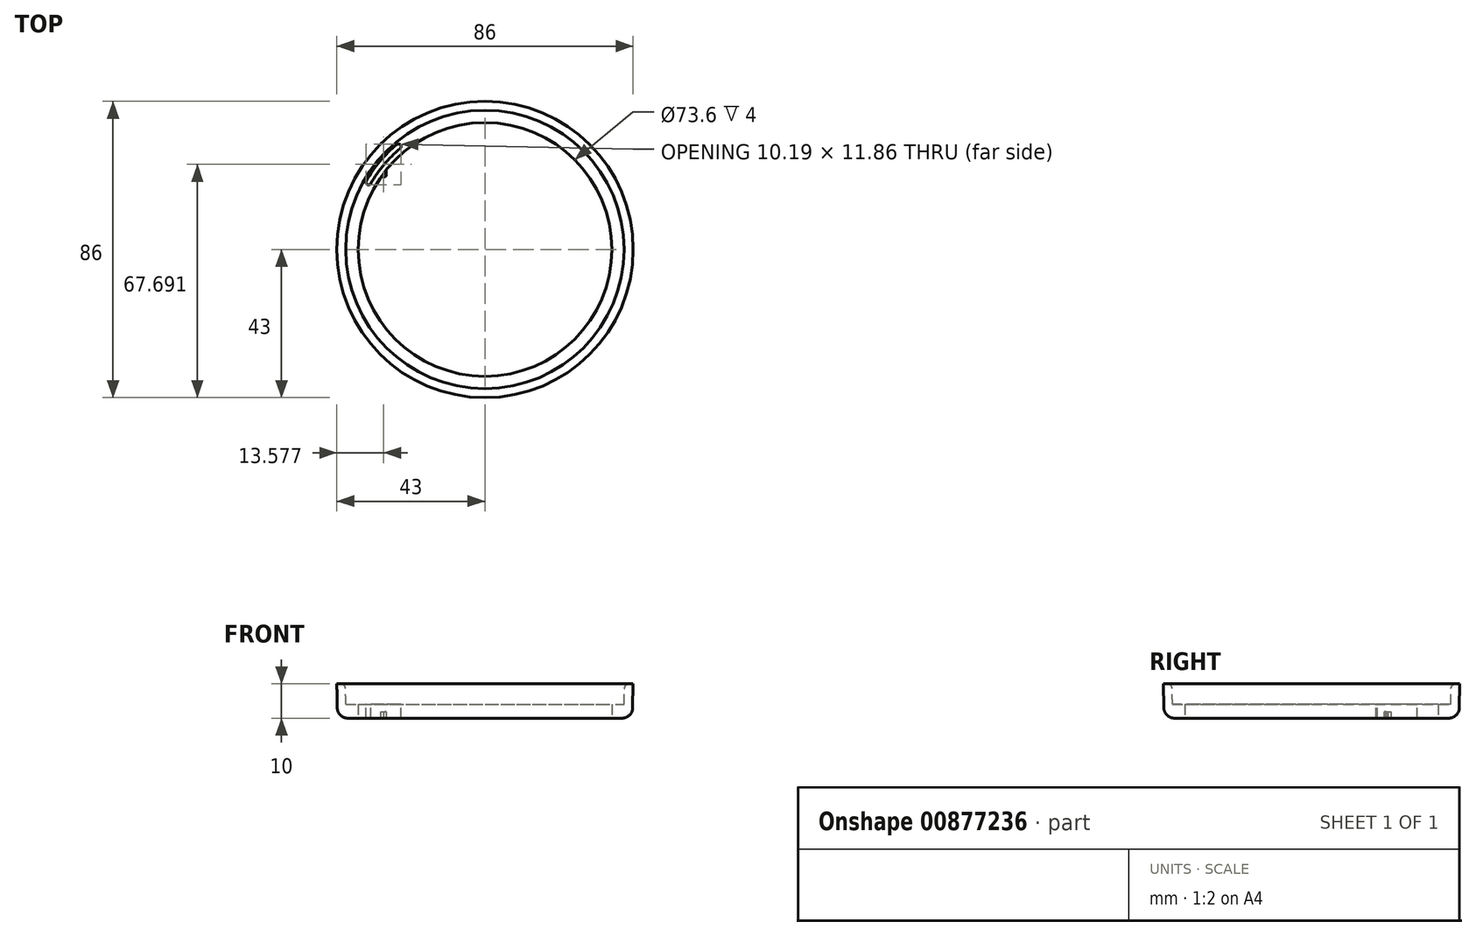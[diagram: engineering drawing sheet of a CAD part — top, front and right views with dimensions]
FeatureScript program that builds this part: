
annotation { "Feature Type Name" : "Feature", "Feature Type Description" : "" }
export const myFeature = defineFeature(function(context is Context, id is Id, definition is map)
    precondition{}
    {
        {
            var Q0;
            Q0=qCreatedBy(makeId("Front.planeOp"),FACE);
            var sketch = newSketch(context, id + "F0", { "sketchPlane" : qUnion([Q0])});
            skLineSegment(sketch, "E0", {"start": v(-42.86, 2.94) * mm, "end": v(-43, 10) * mm});
            skLineSegment(sketch, "E1", {"start": v(-43, 10) * mm, "end": v(-41.97, 10) * mm});
            skLineSegment(sketch, "E2", {"start": v(-40.47, 8.53) * mm, "end": v(-40.38, 4) * mm});
            skLineSegment(sketch, "E3", {"start": v(-40.38, 4) * mm, "end": v(-36.8, 4) * mm});
            skLineSegment(sketch, "E4", {"start": v(-36.8, 4) * mm, "end": v(-36.8, 0) * mm});
            skLineSegment(sketch, "E5", {"start": v(-36.8, 0) * mm, "end": v(-39.86, 0) * mm});
            skLineSegment(sketch, "E6", {"start": v(0, 0) * mm, "end": v(0, 62.72) * mm, "construction": true});
            skPoint(sketch, "E7.visualSharp", {"position": v(-42.8, 0) * mm});
            skArc(sketch, "E7.filletArc", {"start": v(-42.86, 2.94) * mm, "mid": v(-41.96, 0.86) * mm, "end": v(-39.86, 0) * mm});
            skPoint(sketch, "E8.visualSharp", {"position": v(-40.5, 10) * mm});
            skArc(sketch, "E8.filletArc", {"start": v(-40.47, 8.53) * mm, "mid": v(-40.92, 9.57) * mm, "end": v(-41.97, 10) * mm});
            skSolve(sketch);
        }
        {
            var Q0;
            Q0=qSketchRegion(id+"F0",true);
            var Q1;
            Q1=sQuery(id+"F0.wireOp",EDGE,"E6");
            revolve(context, id + "F1", {"entities" : qUnion([Q0]), "axis" : qUnion([Q1]), "revolveType" : RevolveType.FULL});
        }
        {
            var Q0;
            Q0=makeQuery(id+"F1.opRevolve","SWEPT_FACE",FACE,{"disambiguationData":[OSD([sQuery(id+"F0.wireOp",EDGE,"E3")])]});
            var sketch = newSketch(context, id + "F2", { "sketchPlane" : qUnion([Q0])});
            skLineSegment(sketch, "E9", {"start": v(-18.25, 30.04) * mm, "end": v(-19.1, 31.45) * mm});
            skLineSegment(sketch, "E10", {"start": v(0, 0) * mm, "end": v(-18.25, 30.04) * mm, "construction": true});
            skArc(sketch, "E11", {"start": v(-18.25, 30.04) * mm, "mid": v(-0.51, -35.15) * mm, "end": v(19.12, 29.5) * mm, "construction": true});
            skArc(sketch, "E12", {"start": v(19.1, 31.45) * mm, "mid": v(-19.56, -31.17) * mm, "end": v(20.02, 30.88) * mm});
            skArc(sketch, "E13", {"start": v(20.02, 30.88) * mm, "mid": v(0.54, 36.8) * mm, "end": v(-19.1, 31.45) * mm});
            skLineSegment(sketch, "E14", {"start": v(0, 0) * mm, "end": v(0, 32.81) * mm, "construction": true});
            skArc(sketch, "E15.0", {"start": v(-3.13, 35.16) * mm, "mid": v(-8.6, 34.24) * mm, "end": v(-13.87, 32.46) * mm});
            skLineSegment(sketch, "E16", {"start": v(-13.87, 32.46) * mm, "end": v(-13.83, 32.37) * mm});
            skLineSegment(sketch, "E17", {"start": v(-13.83, 32.37) * mm, "end": v(0, 0) * mm, "construction": true});
            skArc(sketch, "E18.trimOffspring", {"start": v(-13.83, 32.37) * mm, "mid": v(-16.08, 31.29) * mm, "end": v(-18.25, 30.04) * mm});
            skLineSegment(sketch, "E19", {"start": v(0, 32.81) * mm, "end": v(0, 36.8) * mm, "construction": true});
            skArc(sketch, "E20", {"start": v(0, 36.8) * mm, "mid": v(-1.76, 36.37) * mm, "end": v(-3.13, 35.16) * mm});
            skPoint(sketch, "E21", {"position": v(-3.12, 35.16) * mm});
            skLineSegment(sketch, "E22.MirrorCS", {"start": v(18.25, 30.04) * mm, "end": v(19.1, 31.45) * mm});
            skArc(sketch, "E23.MirrorCS", {"start": v(-20.02, 30.88) * mm, "mid": v(-0.54, 36.8) * mm, "end": v(19.1, 31.45) * mm});
            skArc(sketch, "E24.MirrorCS", {"start": v(3.13, 35.16) * mm, "mid": v(8.6, 34.24) * mm, "end": v(13.87, 32.46) * mm});
            skArc(sketch, "E25.MirrorCS", {"start": v(13.83, 32.37) * mm, "mid": v(16.08, 31.29) * mm, "end": v(18.25, 30.04) * mm});
            skLineSegment(sketch, "E26.MirrorCS", {"start": v(13.87, 32.46) * mm, "end": v(13.83, 32.37) * mm});
            skArc(sketch, "E27.MirrorCS", {"start": v(0, 36.8) * mm, "mid": v(1.76, 36.37) * mm, "end": v(3.13, 35.16) * mm});
            skLineSegment(sketch, "E28", {"start": v(-20.16, 30.78) * mm, "end": v(-20.03, 29.99) * mm});
            skLineSegment(sketch, "E29", {"start": v(-20.51, 29.4) * mm, "end": v(-22.2, 29.34) * mm});
            skArc(sketch, "E30.0", {"start": v(19.1, 31.45) * mm, "mid": v(0, 36.8) * mm, "end": v(-19.1, 31.45) * mm});
            skArc(sketch, "E31.trimOffspring", {"start": v(-20.16, 30.78) * mm, "mid": v(-21.2, 30.08) * mm, "end": v(-22.2, 29.34) * mm});
            skPoint(sketch, "E32.visualSharp", {"position": v(-19.94, 29.43) * mm});
            skArc(sketch, "E32.filletArc", {"start": v(-20.51, 29.4) * mm, "mid": v(-20.14, 29.59) * mm, "end": v(-20.03, 29.99) * mm});
            skSolve(sketch);
        }
        {
            var Q0;
            Q0=makeQuery(id+"F1.opRevolve","SWEPT_FACE",FACE,{"disambiguationData":[OSD([sQuery(id+"F0.wireOp",EDGE,"E5")])]});
            var sketch = newSketch(context, id + "F3", { "sketchPlane" : qUnion([Q0])});
            skLineSegment(sketch, "E33", {"start": v(0, 0) * mm, "end": v(-36.8, 0) * mm, "construction": true});
            skArc(sketch, "E34.0", {"start": v(-35.3, 0) * mm, "mid": v(-35.25, -1.8) * mm, "end": v(-35.12, -3.6) * mm, "construction": true});
            skLineSegment(sketch, "E35", {"start": v(0, 0) * mm, "end": v(-29.59, 19.25) * mm, "construction": true});
            skLineSegment(sketch, "E36", {"start": v(-29.59, 19.25) * mm, "end": v(-30.85, 20.07) * mm});
            skCircle(sketch, "E37.0", {"center": v(0, 0) * mm, "radius": 36.8 * mm});
            skArc(sketch, "E38.0", {"start": v(-30.84, 17.68) * mm, "mid": v(-33.92, 10.65) * mm, "end": v(-35.41, 3.12) * mm});
            skLineSegment(sketch, "E39", {"start": v(-30.63, 17.54) * mm, "end": v(-30.84, 17.68) * mm});
            skArc(sketch, "E40", {"start": v(-35.41, 3.12) * mm, "mid": v(-36.44, 1.7) * mm, "end": v(-36.8, 0) * mm});
            skArc(sketch, "E41.trimOffspring", {"start": v(-35.41, -3.13) * mm, "mid": v(34.5, -8.6) * mm, "end": v(-29.8, 19.39) * mm, "construction": true});
            skLineSegment(sketch, "E42", {"start": v(-29.59, 19.25) * mm, "end": v(-29.59, 19.25) * mm});
            skArc(sketch, "E43", {"start": v(-29.59, 19.25) * mm, "mid": v(-30.12, 18.4) * mm, "end": v(-30.63, 17.54) * mm});
            skArc(sketch, "E44.MirrorCS", {"start": v(-35.3, 0) * mm, "mid": v(33.84, 10.04) * mm, "end": v(-29.59, -19.25) * mm, "construction": true});
            skArc(sketch, "E45.MirrorCS", {"start": v(-30.84, -17.68) * mm, "mid": v(-33.92, -10.65) * mm, "end": v(-35.41, -3.13) * mm});
            skLineSegment(sketch, "E46.MirrorCS", {"start": v(-29.59, -19.25) * mm, "end": v(-30.85, -20.07) * mm});
            skArc(sketch, "E47.MirrorCS", {"start": v(-29.59, -19.25) * mm, "mid": v(-30.12, -18.4) * mm, "end": v(-30.63, -17.54) * mm});
            skLineSegment(sketch, "E48.MirrorCS", {"start": v(-30.63, -17.54) * mm, "end": v(-30.84, -17.68) * mm});
            skArc(sketch, "E49.MirrorCS", {"start": v(-35.41, -3.12) * mm, "mid": v(-36.44, -1.7) * mm, "end": v(-36.8, 0) * mm});
            skArc(sketch, "E50.trimOffspring", {"start": v(-30.63, -17.54) * mm, "mid": v(35.29, -1) * mm, "end": v(-29.59, 19.25) * mm, "construction": true});
            skLineSegment(sketch, "E51", {"start": v(-30.15, -21.1) * mm, "end": v(-29.12, -21.1) * mm});
            skLineSegment(sketch, "E52", {"start": v(-28.62, -21.61) * mm, "end": v(-28.64, -23.1) * mm});
            skPoint(sketch, "E53.visualSharp", {"position": v(-28.6, -21.1) * mm});
            skArc(sketch, "E53.filletArc", {"start": v(-28.62, -21.61) * mm, "mid": v(-28.76, -21.25) * mm, "end": v(-29.12, -21.1) * mm});
            skArc(sketch, "E54", {"start": v(-30.85, 20.07) * mm, "mid": v(36.75, 1.87) * mm, "end": v(-28.64, -23.1) * mm, "construction": true});
            skArc(sketch, "E55", {"start": v(-30.85, -20.07) * mm, "mid": v(-36.8, 0) * mm, "end": v(-30.85, 20.07) * mm});
            skArc(sketch, "E56", {"start": v(-30.15, -21.1) * mm, "mid": v(-30.5, -20.59) * mm, "end": v(-30.85, -20.07) * mm, "construction": true});
            skArc(sketch, "E57", {"start": v(-28.64, -23.1) * mm, "mid": v(-29.41, -22.12) * mm, "end": v(-30.15, -21.1) * mm});
            skSolve(sketch);
        }
        {
            var Q0;
            {var subQ1=sQuery(id+"F3.wireOp",EDGE,"E36");Q0=makeQuery(id+"F3.imprint","IMPRINT",FACE,{"disambiguationData":[TD([[makeQuery(id+"F3.imprint","IMPRINT",EDGE,{"derivedFrom":subQ1}),1.0]])]});}
            var Q1;
            Q1=makeQuery(id+"F3.imprint","IMPRINT",FACE,{"disambiguationData":[TD([[makeQuery(id+"F3.imprint","IMPRINT",EDGE,{"derivedFrom":sQuery(id+"F3.wireOp",EDGE,"E45.MirrorCS")}),1.0]])]});
            var Q2;
            {var subQ0=sQuery(id+"F3.wireOp",EDGE,"E51");Q2=makeQuery(id+"F3.imprint","IMPRINT",FACE,{"disambiguationData":[TD([[makeQuery(id+"F3.imprint","IMPRINT",EDGE,{"derivedFrom":subQ0}),-1.0]])]});}
            extrude(context, id + "F4", {"entities" : qUnion([Q0, Q1, Q2]), "operationType" : NewBodyOperationType.ADD, "oppositeDirection" : true, "offsetDistance" : 25 * mm, "depth" : 1.8 * mm});
        }
        {
            var Q0;
            {var subQ6=sQuery(id+"F2.wireOp",EDGE,"E31.trimOffspring");Q0=makeQuery(id+"F2.imprint","IMPRINT",FACE,{"disambiguationData":[TD([[makeQuery(id+"F2.imprint","IMPRINT",EDGE,{"derivedFrom":subQ6}),1.0]])]});}
            var sketch = newSketch(context, id + "F5", { "sketchPlane" : qUnion([Q0])});
            skLineSegment(sketch, "E58", {"start": v(0, 0) * mm, "end": v(-25.07, 29.88) * mm, "construction": true});
            skLineSegment(sketch, "E59", {"start": v(0, 0) * mm, "end": v(-33.77, 19.5) * mm, "construction": true});
            skArc(sketch, "E60", {"start": v(-25.07, 29.88) * mm, "mid": v(29.88, -25.07) * mm, "end": v(-33.77, 19.5) * mm, "construction": true});
            skArc(sketch, "E61", {"start": v(-33.77, 19.5) * mm, "mid": v(-29.9, 25.1) * mm, "end": v(-25.07, 29.88) * mm, "construction": true});
            skArc(sketch, "E62.0.startCap", {"start": v(-33.12, 19.13) * mm, "mid": v(-34.14, 18.85) * mm, "end": v(-34.43, 19.87) * mm});
            skArc(sketch, "E62.0.endCap", {"start": v(-25.54, 30.46) * mm, "mid": v(-24.49, 30.35) * mm, "end": v(-24.6, 29.3) * mm});
            skArc(sketch, "E62.0.left", {"start": v(-34.43, 19.87) * mm, "mid": v(-30.48, 25.58) * mm, "end": v(-25.54, 30.46) * mm});
            skArc(sketch, "E62.0.right", {"start": v(-33.12, 19.13) * mm, "mid": v(-29.33, 24.61) * mm, "end": v(-24.6, 29.3) * mm});
            skSolve(sketch);
        }
        {
            var Q0;
            Q0=qSketchRegion(id+"F5",true);
            extrude(context, id + "F6", {"entities" : qUnion([Q0]), "operationType" : NewBodyOperationType.REMOVE, "endBound" : BoundingType.THROUGH_ALL, "oppositeDirection" : true, "depth" : 25 * mm});
        }
    });
